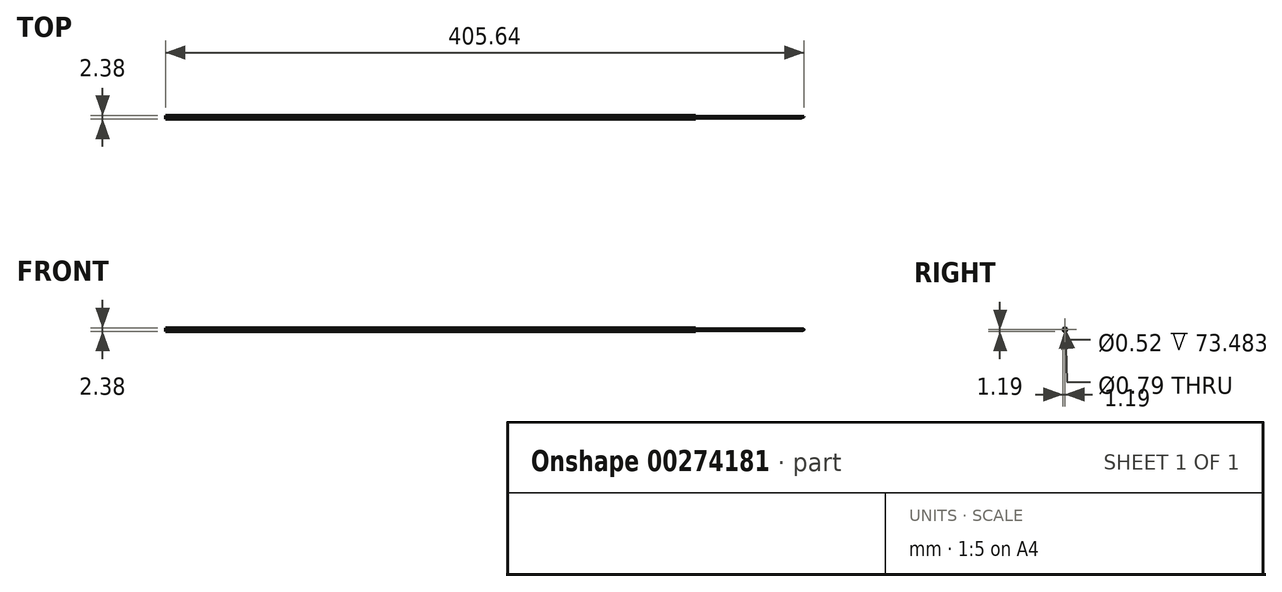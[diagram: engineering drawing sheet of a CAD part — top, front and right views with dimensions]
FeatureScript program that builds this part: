
annotation { "Feature Type Name" : "Feature", "Feature Type Description" : "" }
export const myFeature = defineFeature(function(context is Context, id is Id, definition is map)
    precondition{}
    {
        {
            var Q0;
            Q0=qCreatedBy(makeId("Right.planeOp"),FACE);
            var sketch = newSketch(context, id + "F0", { "sketchPlane" : qUnion([Q0])});
            skCircle(sketch, "E0", {"center": v(0, 0) * mm, "radius": 0.4 * mm});
            skCircle(sketch, "E1", {"center": v(0, 0) * mm, "radius": 1.2 * mm});
            skSolve(sketch);
        }
        {
            var Q0;
            Q0 = qSketchRegion(id + "F0", true);
            extrude(context, id + "F1", {"entities" : qUnion([Q0]), "oppositeDirection" : true, "depth" : 336.55 * mm});
        }
        {
            var Q0;
            Q0=makeQuery(id+"F1.opExtrude","CAP_FACE",FACE,{"disambiguationData":[OSD([sQuery(id+"F0.wireOp",EDGE,"E0"),sQuery(id+"F0.wireOp",EDGE,"E1")])],"isStart":true});
            var sketch = newSketch(context, id + "F2", { "sketchPlane" : qUnion([Q0])});
            skCircle(sketch, "E2", {"center": v(0, 0) * mm, "radius": 0.4 * mm});
            skCircle(sketch, "E3", {"center": v(0, 0) * mm, "radius": 0.26 * mm});
            skSolve(sketch);
        }
        {
            var Q0;
            Q0=makeQuery(id+"F2.imprint","IMPRINT",FACE,{"disambiguationData":[TD([[makeQuery(id+"F2.imprint","IMPRINT",EDGE,{"derivedFrom":sQuery(id+"F2.wireOp",EDGE,"E3")}),-1.0]])]});
            extrude(context, id + "F3", {"entities" : qUnion([Q0]), "depth" : 69.1 * mm, "hasSecondDirection" : true, "secondDirectionOppositeDirection" : true, "secondDirectionDepth" : 4.83 * mm});
        }
        {
            var Q0;
            Q0=qCreatedBy(makeId("Top.planeOp"),FACE);
            var sketch = newSketch(context, id + "F4", { "sketchPlane" : qUnion([Q0])});
            skArc(sketch, "E4", {"start": v(69.09, 0.4) * mm, "mid": v(68.1, 0.03) * mm, "end": v(67.18, -0.5) * mm});
            skLineSegment(sketch, "E5", {"start": v(67.18, -0.5) * mm, "end": v(69.09, -0.5) * mm});
            skLineSegment(sketch, "E6", {"start": v(69.09, -0.5) * mm, "end": v(69.09, 0.4) * mm});
            skSolve(sketch);
        }
        {
            var Q0;
            Q0=makeQuery(id+"F4.imprint","IMPRINT",FACE,{"disambiguationData":[TD([[makeQuery(id+"F4.imprint","IMPRINT",EDGE,{"derivedFrom":sQuery(id+"F4.wireOp",EDGE,"E4")}),1.0]])]});
            extrude(context, id + "F5", {"entities" : qUnion([Q0]), "operationType" : NewBodyOperationType.REMOVE, "endBound" : BoundingType.SYMMETRIC, "depth" : 25.4 * mm});
        }
    });
